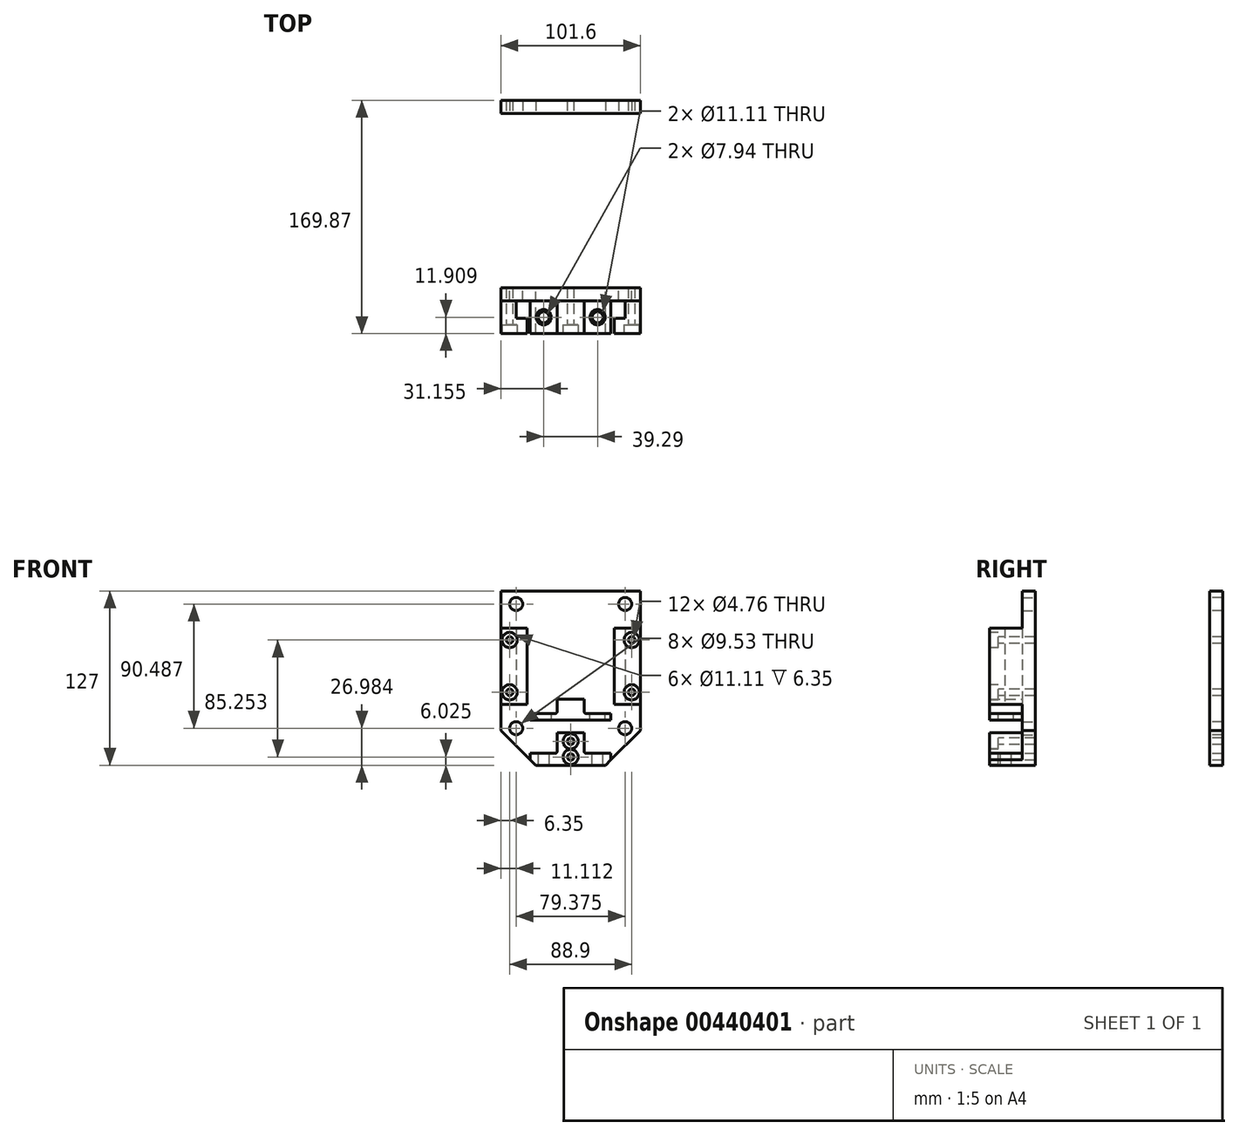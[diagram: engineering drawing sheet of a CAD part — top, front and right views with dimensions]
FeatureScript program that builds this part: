
annotation { "Feature Type Name" : "Feature", "Feature Type Description" : "" }
export const myFeature = defineFeature(function(context is Context, id is Id, definition is map)
    precondition{}
    {
        {
            var Q0;
            Q0=qCreatedBy(makeId("Front.planeOp"),FACE);
            var sketch = newSketch(context, id + "F0", { "sketchPlane" : qUnion([Q0])});
            skLineSegment(sketch, "E0.bottom", {"start": v(-50.8, 47.95) * mm, "end": v(50.8, 47.95) * mm});
            skLineSegment(sketch, "E0.top", {"start": v(-25.4, -79.05) * mm, "end": v(25.4, -79.05) * mm});
            skLineSegment(sketch, "E0.left", {"start": v(-50.8, 47.95) * mm, "end": v(-50.8, -53.65) * mm});
            skLineSegment(sketch, "E0.right", {"start": v(50.8, 47.95) * mm, "end": v(50.8, -53.65) * mm});
            skLineSegment(sketch, "E1", {"start": v(-50.8, -53.65) * mm, "end": v(-25.4, -79.05) * mm});
            skLineSegment(sketch, "E2", {"start": v(25.4, -79.05) * mm, "end": v(50.8, -53.65) * mm});
            skCircle(sketch, "E3", {"center": v(-39.69, 38.42) * mm, "radius": 4.76 * mm});
            skCircle(sketch, "E4", {"center": v(39.69, 38.42) * mm, "radius": 4.76 * mm});
            skCircle(sketch, "E5", {"center": v(39.69, -52.07) * mm, "radius": 4.76 * mm});
            skCircle(sketch, "E6", {"center": v(-39.69, -52.07) * mm, "radius": 4.76 * mm});
            skSolve(sketch);
        }
        {
            var Q0;
            Q0 = qSketchRegion(id + "F0", true);
            extrude(context, id + "F1", {"entities" : qUnion([Q0]), "depth" : 9.52 * mm});
        }
        {
            var Q0;
            Q0=makeQuery(id+"F1.opExtrude","CAP_FACE",FACE,{"disambiguationData":[OSD([sQuery(id+"F0.wireOp",EDGE,"E0.bottom"),sQuery(id+"F0.wireOp",EDGE,"E0.top"),sQuery(id+"F0.wireOp",EDGE,"E0.left"),sQuery(id+"F0.wireOp",EDGE,"E0.right"),sQuery(id+"F0.wireOp",EDGE,"E1"),sQuery(id+"F0.wireOp",EDGE,"E2"),sQuery(id+"F0.wireOp",EDGE,"E3"),sQuery(id+"F0.wireOp",EDGE,"E4"),sQuery(id+"F0.wireOp",EDGE,"E5"),sQuery(id+"F0.wireOp",EDGE,"E6")])],"isStart":false});
            var sketch = newSketch(context, id + "F2", { "sketchPlane" : qUnion([Q0])});
            skLineSegment(sketch, "E7.bottom", {"start": v(-50.8, 20.96) * mm, "end": v(-39.69, 20.96) * mm});
            skLineSegment(sketch, "E7.top", {"start": v(-50.8, -34.6) * mm, "end": v(-39.69, -34.6) * mm});
            skLineSegment(sketch, "E7.left", {"start": v(-50.8, 20.96) * mm, "end": v(-50.8, -34.6) * mm});
            skLineSegment(sketch, "E7.right", {"start": v(-39.69, 20.96) * mm, "end": v(-39.69, -34.6) * mm});
            skLineSegment(sketch, "E8.MirrorCS", {"start": v(39.69, 20.96) * mm, "end": v(39.69, -34.6) * mm});
            skLineSegment(sketch, "E9.MirrorCS", {"start": v(50.8, 20.96) * mm, "end": v(50.8, -34.6) * mm});
            skLineSegment(sketch, "E10.MirrorCS", {"start": v(50.8, 20.96) * mm, "end": v(39.69, 20.96) * mm});
            skLineSegment(sketch, "E11.MirrorCS", {"start": v(50.8, -34.6) * mm, "end": v(39.69, -34.6) * mm});
            skLineSegment(sketch, "E12.bottom", {"start": v(-29.37, -41.35) * mm, "end": v(-11.2, -41.35) * mm});
            skLineSegment(sketch, "E12.top", {"start": v(-29.37, -46.12) * mm, "end": v(29.37, -46.12) * mm});
            skLineSegment(sketch, "E12.left", {"start": v(-29.37, -41.35) * mm, "end": v(-29.37, -46.12) * mm});
            skLineSegment(sketch, "E12.right", {"start": v(29.37, -41.35) * mm, "end": v(29.37, -46.12) * mm});
            skLineSegment(sketch, "E13.bottom", {"start": v(-9.92, -31.04) * mm, "end": v(9.92, -31.04) * mm});
            skLineSegment(sketch, "E13.left", {"start": v(-9.92, -31.04) * mm, "end": v(-9.92, -40.08) * mm});
            skLineSegment(sketch, "E13.right", {"start": v(9.92, -31.04) * mm, "end": v(9.92, -40.08) * mm});
            skLineSegment(sketch, "E14.trimOffspring", {"start": v(11.2, -41.35) * mm, "end": v(29.37, -41.35) * mm});
            skLineSegment(sketch, "E15", {"start": v(-29.37, -75.08) * mm, "end": v(-25.4, -79.05) * mm});
            skLineSegment(sketch, "E16", {"start": v(-25.4, -79.05) * mm, "end": v(25.4, -79.05) * mm});
            skLineSegment(sketch, "E17", {"start": v(25.4, -79.05) * mm, "end": v(29.37, -75.08) * mm});
            skLineSegment(sketch, "E18", {"start": v(29.37, -75.08) * mm, "end": v(29.37, -70.32) * mm});
            skLineSegment(sketch, "E19", {"start": v(29.37, -70.32) * mm, "end": v(11.2, -70.32) * mm});
            skLineSegment(sketch, "E20", {"start": v(9.92, -69.05) * mm, "end": v(9.92, -55.24) * mm});
            skLineSegment(sketch, "E21", {"start": v(9.92, -55.24) * mm, "end": v(-9.92, -55.24) * mm});
            skLineSegment(sketch, "E22", {"start": v(-9.92, -55.24) * mm, "end": v(-9.92, -69.05) * mm});
            skLineSegment(sketch, "E23", {"start": v(-11.2, -70.32) * mm, "end": v(-29.37, -70.32) * mm});
            skLineSegment(sketch, "E24", {"start": v(-29.37, -70.32) * mm, "end": v(-29.37, -75.08) * mm});
            skPoint(sketch, "E25.visualSharp", {"position": v(9.92, -41.35) * mm});
            skArc(sketch, "E25.filletArc", {"start": v(9.92, -40.08) * mm, "mid": v(10.3, -40.98) * mm, "end": v(11.2, -41.35) * mm});
            skPoint(sketch, "E26.visualSharp", {"position": v(-9.92, -41.35) * mm});
            skArc(sketch, "E26.filletArc", {"start": v(-11.2, -41.35) * mm, "mid": v(-10.3, -40.98) * mm, "end": v(-9.92, -40.08) * mm});
            skPoint(sketch, "E27.visualSharp", {"position": v(9.92, -70.32) * mm});
            skArc(sketch, "E27.filletArc", {"start": v(9.92, -69.05) * mm, "mid": v(10.3, -69.95) * mm, "end": v(11.2, -70.32) * mm});
            skPoint(sketch, "E28.visualSharp", {"position": v(-9.92, -70.32) * mm});
            skArc(sketch, "E28.filletArc", {"start": v(-11.2, -70.32) * mm, "mid": v(-10.3, -69.95) * mm, "end": v(-9.92, -69.05) * mm});
            skSolve(sketch);
        }
        {
            var Q0;
            Q0 = qSketchRegion(id + "F2", true);
            extrude(context, id + "F3", {"entities" : qUnion([Q0]), "operationType" : NewBodyOperationType.ADD, "depth" : 23.8 * mm});
        }
        {
            var Q0;
            Q0=makeQuery(id+"F3.opExtrude","SWEPT_FACE",FACE,{"disambiguationData":[OSD([sQuery(id+"F2.wireOp",EDGE,"E7.right")])]});
            var sketch = newSketch(context, id + "F4", { "sketchPlane" : qUnion([Q0])});
            skLineSegment(sketch, "E29.bottom", {"start": v(-33.34, 20.96) * mm, "end": v(-22.23, 20.96) * mm});
            skLineSegment(sketch, "E29.top", {"start": v(-33.34, -34.6) * mm, "end": v(-22.23, -34.6) * mm});
            skLineSegment(sketch, "E29.left", {"start": v(-33.34, 20.96) * mm, "end": v(-33.34, -34.6) * mm});
            skLineSegment(sketch, "E29.right", {"start": v(-22.23, 20.96) * mm, "end": v(-22.23, -34.6) * mm});
            skSolve(sketch);
        }
        {
            var Q0;
            Q0 = qSketchRegion(id + "F4", true);
            extrude(context, id + "F5", {"entities" : qUnion([Q0]), "operationType" : NewBodyOperationType.ADD, "depth" : 7.94 * mm});
        }
        {
            var Q0;
            Q0=makeQuery(id+"F3.opExtrude","SWEPT_FACE",FACE,{"disambiguationData":[OSD([sQuery(id+"F2.wireOp",EDGE,"E8.MirrorCS")])]});
            var sketch = newSketch(context, id + "F6", { "sketchPlane" : qUnion([Q0])});
            skLineSegment(sketch, "E30.bottom", {"start": v(33.34, 20.96) * mm, "end": v(22.22, 20.96) * mm});
            skLineSegment(sketch, "E30.top", {"start": v(33.34, -34.6) * mm, "end": v(22.23, -34.6) * mm});
            skLineSegment(sketch, "E30.left", {"start": v(33.34, 20.96) * mm, "end": v(33.34, -34.6) * mm});
            skLineSegment(sketch, "E30.right", {"start": v(22.22, 20.96) * mm, "end": v(22.23, -34.6) * mm});
            skSolve(sketch);
        }
        {
            var Q0;
            Q0 = qSketchRegion(id + "F6", true);
            extrude(context, id + "F7", {"entities" : qUnion([Q0]), "operationType" : NewBodyOperationType.ADD, "depth" : 7.94 * mm});
        }
        {
            var Q0;
            Q0=makeQuery(id+"F5.boolean.opBoolean","MERGE",FACE,{"derivedFrom":[makeQuery(id+"F3.opExtrude","CAP_FACE",FACE,{"disambiguationData":[OSD([sQuery(id+"F2.wireOp",EDGE,"E7.bottom"),sQuery(id+"F2.wireOp",EDGE,"E7.top"),sQuery(id+"F2.wireOp",EDGE,"E7.left"),sQuery(id+"F2.wireOp",EDGE,"E7.right")])],"isStart":false}),makeQuery(id+"F5.opExtrude","SWEPT_FACE",FACE,{"disambiguationData":[OSD([sQuery(id+"F4.wireOp",EDGE,"E29.left")])]})]});
            var sketch = newSketch(context, id + "F8", { "sketchPlane" : qUnion([Q0])});
            skCircle(sketch, "E31", {"center": v(-44.45, 12.23) * mm, "radius": 5.56 * mm});
            skCircle(sketch, "E32", {"center": v(-44.45, -25.87) * mm, "radius": 5.56 * mm});
            skCircle(sketch, "E33.MirrorC", {"center": v(44.45, 12.23) * mm, "radius": 5.56 * mm});
            skCircle(sketch, "E34.MirrorC", {"center": v(44.45, -25.87) * mm, "radius": 5.56 * mm});
            skCircle(sketch, "E35", {"center": v(0, -73.03) * mm, "radius": 5.56 * mm});
            skCircle(sketch, "E36", {"center": v(0, -61.6) * mm, "radius": 5.56 * mm});
            skSolve(sketch);
        }
        {
            var Q0;
            Q0 = qSketchRegion(id + "F8", true);
            extrude(context, id + "F9", {"entities" : qUnion([Q0]), "operationType" : NewBodyOperationType.REMOVE, "oppositeDirection" : true, "depth" : 6.35 * mm});
        }
        {
            var Q0;
            Q0=makeQuery(id+"F9.boolean.opBoolean","COPY",FACE,{"derivedFrom":makeQuery(id+"F9.opExtrude","CAP_FACE",FACE,{"disambiguationData":[OSD([sQuery(id+"F8.wireOp",EDGE,"E32")])],"isStart":false})});
            var sketch = newSketch(context, id + "F10", { "sketchPlane" : qUnion([Q0])});
            skCircle(sketch, "E37", {"center": v(-44.45, -25.87) * mm, "radius": 2.38 * mm});
            skCircle(sketch, "E38", {"center": v(-44.45, 12.23) * mm, "radius": 2.38 * mm});
            skCircle(sketch, "E39.MirrorC", {"center": v(44.45, -25.87) * mm, "radius": 2.38 * mm});
            skCircle(sketch, "E40.MirrorC", {"center": v(44.45, 12.23) * mm, "radius": 2.38 * mm});
            skCircle(sketch, "E41", {"center": v(0, -61.6) * mm, "radius": 2.38 * mm});
            skCircle(sketch, "E42", {"center": v(0, -73.03) * mm, "radius": 2.38 * mm});
            skSolve(sketch);
        }
        {
            var Q0;
            Q0 = qSketchRegion(id + "F10", true);
            extrude(context, id + "F11", {"entities" : qUnion([Q0]), "operationType" : NewBodyOperationType.REMOVE, "oppositeDirection" : true, "depth" : 50.8 * mm});
        }
        {
            var Q0;
            Q0=makeQuery(id+"F3.opExtrude","SWEPT_FACE",FACE,{"disambiguationData":[OSD([sQuery(id+"F2.wireOp",EDGE,"E12.bottom")])]});
            var sketch = newSketch(context, id + "F12", { "sketchPlane" : qUnion([Q0])});
            skCircle(sketch, "E43", {"center": v(-19.64, -21.43) * mm, "radius": 5.56 * mm});
            skCircle(sketch, "E44.MirrorC", {"center": v(19.64, -21.43) * mm, "radius": 5.56 * mm});
            skSolve(sketch);
        }
        {
            var Q0;
            Q0 = qSketchRegion(id + "F12", true);
            extrude(context, id + "F13", {"entities" : qUnion([Q0]), "operationType" : NewBodyOperationType.REMOVE, "oppositeDirection" : true, "depth" : 6.35 * mm});
        }
        {
            var Q0;
            Q0=makeQuery(id+"F3.opExtrude","SWEPT_FACE",FACE,{"disambiguationData":[OSD([sQuery(id+"F2.wireOp",EDGE,"E23")])]});
            var sketch = newSketch(context, id + "F14", { "sketchPlane" : qUnion([Q0])});
            skCircle(sketch, "E45", {"center": v(-19.64, -21.43) * mm, "radius": 3.97 * mm});
            skPoint(sketch, "E45.centerSnap0", {"position": v(-11.2, -21.43) * mm});
            skPoint(sketch, "E46.MirrorP", {"position": v(11.2, -21.43) * mm});
            skCircle(sketch, "E47.MirrorC", {"center": v(19.64, -21.43) * mm, "radius": 3.97 * mm});
            skSolve(sketch);
        }
        {
            var Q0;
            Q0 = qSketchRegion(id + "F14", true);
            extrude(context, id + "F15", {"entities" : qUnion([Q0]), "operationType" : NewBodyOperationType.REMOVE, "oppositeDirection" : true, "depth" : 25.4 * mm});
        }
        {
            var Q0;
            Q0=qCreatedBy(makeId("Front.planeOp"),FACE);
            cPlane(context, id + "F16", {"entities" : qUnion([Q0]), "cplaneType" : CPlaneType.OFFSET, "offset" : 127 * mm, "oppositeDirection" : true, "width" : 152.4 * mm, "height" : 152.4 * mm});
        }
        {
            var Q0;
            Q0=qCreatedBy(id+"F16.planeOp",FACE);
            var sketch = newSketch(context, id + "F17", { "sketchPlane" : qUnion([Q0])});
            skLineSegment(sketch, "E48", {"start": v(-50.8, 47.95) * mm, "end": v(-50.8, -53.65) * mm});
            skLineSegment(sketch, "E49", {"start": v(-50.8, -53.65) * mm, "end": v(-25.4, -79.05) * mm});
            skLineSegment(sketch, "E50", {"start": v(-25.4, -79.05) * mm, "end": v(25.4, -79.05) * mm});
            skLineSegment(sketch, "E51", {"start": v(25.4, -79.05) * mm, "end": v(50.8, -53.65) * mm});
            skLineSegment(sketch, "E52", {"start": v(50.8, -53.65) * mm, "end": v(50.8, 47.95) * mm});
            skLineSegment(sketch, "E53", {"start": v(50.8, 47.95) * mm, "end": v(-50.8, 47.95) * mm});
            skCircle(sketch, "E54", {"center": v(-39.69, 38.42) * mm, "radius": 4.76 * mm});
            skCircle(sketch, "E55", {"center": v(39.69, 38.42) * mm, "radius": 4.76 * mm});
            skCircle(sketch, "E56", {"center": v(44.45, 12.23) * mm, "radius": 2.38 * mm});
            skCircle(sketch, "E57", {"center": v(44.45, -25.87) * mm, "radius": 2.38 * mm});
            skCircle(sketch, "E58", {"center": v(-44.45, -25.87) * mm, "radius": 2.38 * mm});
            skCircle(sketch, "E59", {"center": v(-44.45, 12.23) * mm, "radius": 2.38 * mm});
            skCircle(sketch, "E60", {"center": v(-39.69, -52.07) * mm, "radius": 4.76 * mm});
            skCircle(sketch, "E61", {"center": v(39.69, -52.07) * mm, "radius": 4.76 * mm});
            skCircle(sketch, "E62", {"center": v(0, -61.6) * mm, "radius": 2.38 * mm});
            skCircle(sketch, "E63", {"center": v(0, -73.03) * mm, "radius": 2.38 * mm});
            skSolve(sketch);
        }
        {
            var Q0;
            Q0 = qSketchRegion(id + "F17", true);
            extrude(context, id + "F18", {"entities" : qUnion([Q0]), "oppositeDirection" : true, "depth" : 9.52 * mm});
        }
    });
